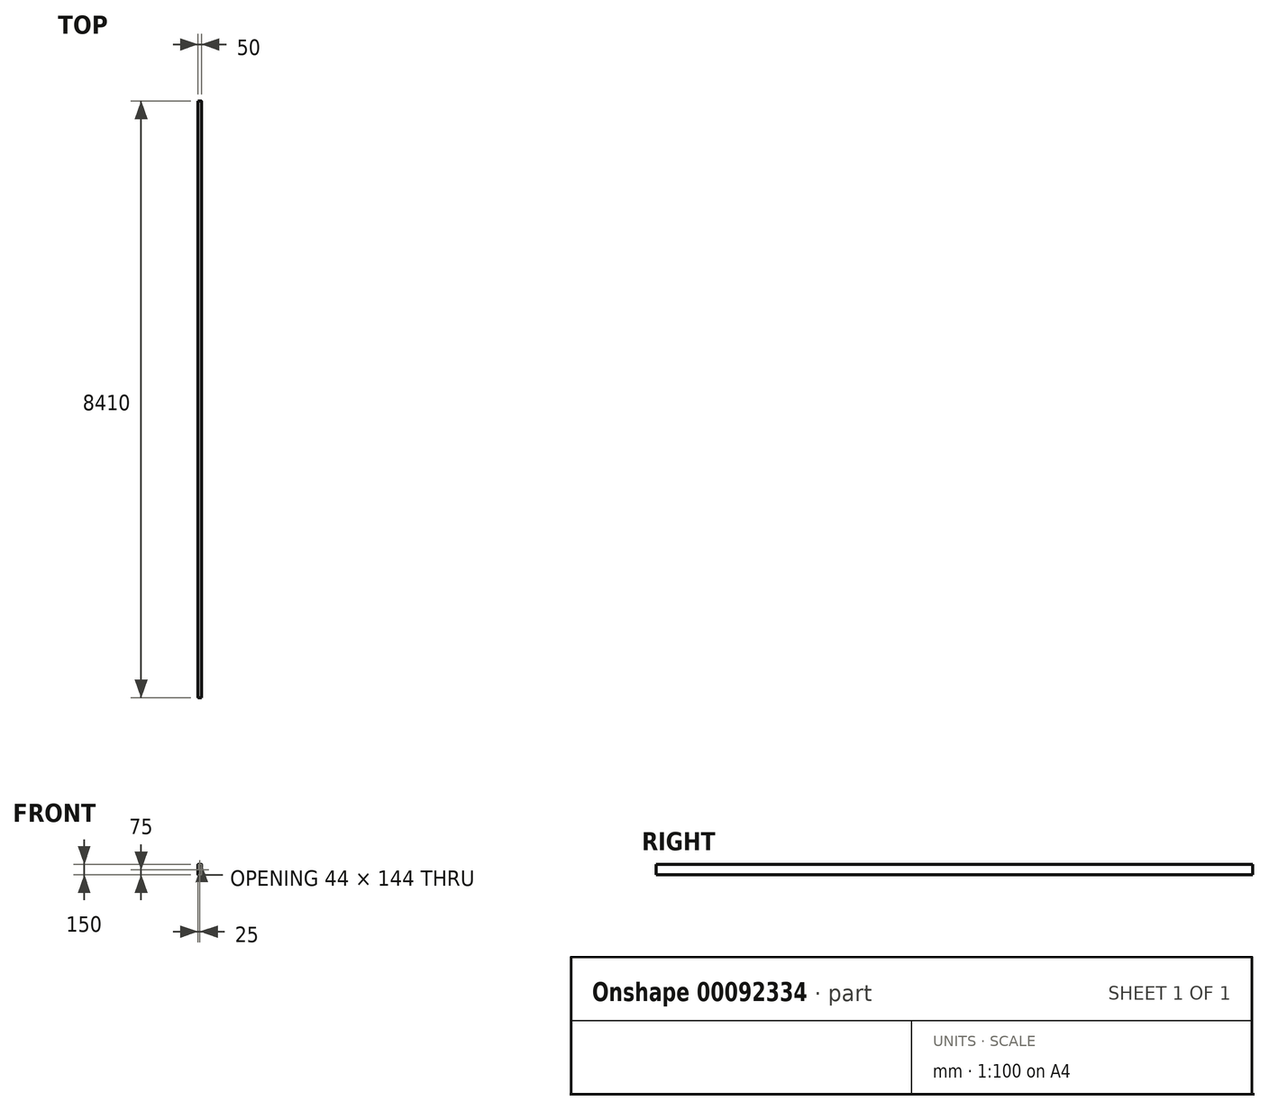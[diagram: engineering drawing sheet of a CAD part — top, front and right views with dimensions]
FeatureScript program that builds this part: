
annotation { "Feature Type Name" : "Feature", "Feature Type Description" : "" }
export const myFeature = defineFeature(function(context is Context, id is Id, definition is map)
    precondition{}
    {
        {
            var Q0;
            Q0=qCreatedBy(makeId("Front.planeOp"),FACE);
            var sketch = newSketch(context, id + "F0", { "sketchPlane" : qUnion([Q0])});
            skLineSegment(sketch, "E0.bottom", {"start": v(2.4, 0) * mm, "end": v(47.6, 0) * mm});
            skLineSegment(sketch, "E0.top", {"start": v(2.4, 150) * mm, "end": v(47.6, 150) * mm});
            skLineSegment(sketch, "E0.left", {"start": v(0, 2.4) * mm, "end": v(0, 147.6) * mm});
            skLineSegment(sketch, "E0.right", {"start": v(50, 2.4) * mm, "end": v(50, 147.6) * mm});
            skPoint(sketch, "E1.visualSharp", {"position": v(0, 150) * mm});
            skArc(sketch, "E1.filletArc", {"start": v(2.4, 150) * mm, "mid": v(0.7, 149.3) * mm, "end": v(0, 147.6) * mm});
            skPoint(sketch, "E2.visualSharp", {"position": v(50, 150) * mm});
            skArc(sketch, "E2.filletArc", {"start": v(50, 147.6) * mm, "mid": v(49.3, 149.3) * mm, "end": v(47.6, 150) * mm});
            skPoint(sketch, "E3.visualSharp", {"position": v(0, 0) * mm});
            skArc(sketch, "E3.filletArc", {"start": v(0, 2.4) * mm, "mid": v(0.7, 0.7) * mm, "end": v(2.4, 0) * mm});
            skPoint(sketch, "E4.visualSharp", {"position": v(50, 0) * mm});
            skArc(sketch, "E4.filletArc", {"start": v(47.6, 0) * mm, "mid": v(49.3, 0.7) * mm, "end": v(50, 2.4) * mm});
            skLineSegment(sketch, "E5.0", {"start": v(3, 5.4) * mm, "end": v(3, 144.6) * mm});
            skLineSegment(sketch, "E6.0", {"start": v(5.4, 147) * mm, "end": v(44.6, 147) * mm});
            skLineSegment(sketch, "E7.0", {"start": v(47, 5.4) * mm, "end": v(47, 144.6) * mm});
            skLineSegment(sketch, "E8.0", {"start": v(5.4, 3) * mm, "end": v(44.6, 3) * mm});
            skArc(sketch, "E9.filletArc", {"start": v(5.4, 147) * mm, "mid": v(3.7, 146.3) * mm, "end": v(3, 144.6) * mm});
            skArc(sketch, "E10.filletArc", {"start": v(3, 5.4) * mm, "mid": v(3.7, 3.7) * mm, "end": v(5.4, 3) * mm});
            skArc(sketch, "E11.filletArc", {"start": v(47, 144.6) * mm, "mid": v(46.3, 146.3) * mm, "end": v(44.6, 147) * mm});
            skArc(sketch, "E12.filletArc", {"start": v(44.6, 3) * mm, "mid": v(46.3, 3.7) * mm, "end": v(47, 5.4) * mm});
            skSolve(sketch);
        }
        {
            var Q0;
            Q0 = qSketchRegion(id + "F0", true);
            extrude(context, id + "F1", {"entities" : qUnion([Q0]), "depth" : 8410 * mm, "offsetDistance" : 25 * mm});
        }
    });
